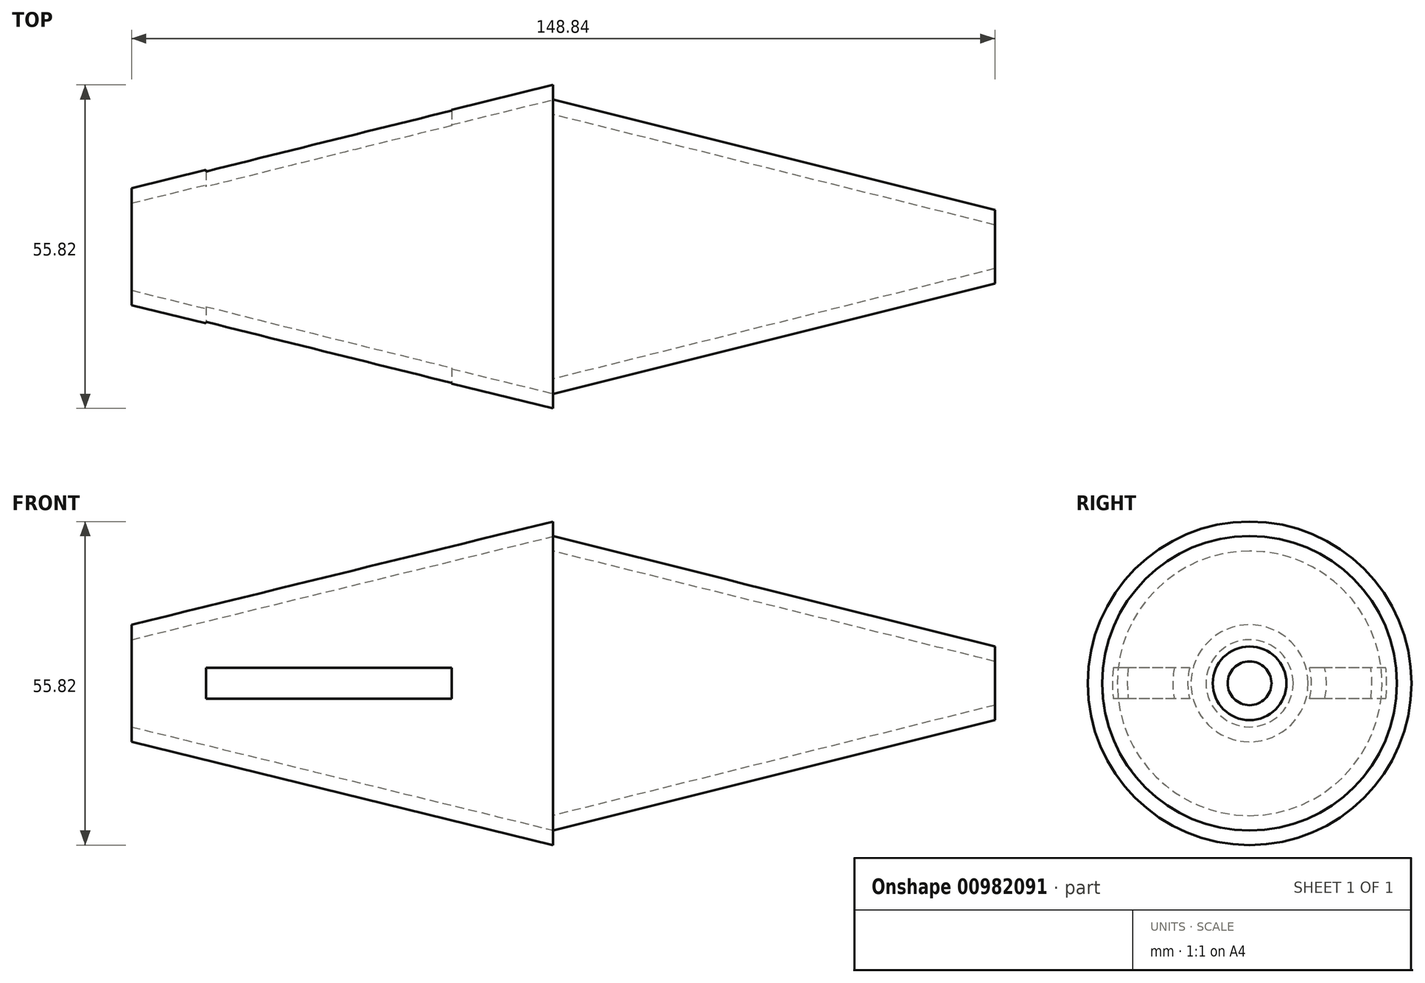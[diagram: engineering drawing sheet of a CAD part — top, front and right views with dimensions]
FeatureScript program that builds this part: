
annotation { "Feature Type Name" : "Feature", "Feature Type Description" : "" }
export const myFeature = defineFeature(function(context is Context, id is Id, definition is map)
    precondition{}
    {
        {
            var Q0;
            Q0=qCreatedBy(makeId("Front.planeOp"),FACE);
            var sketch = newSketch(context, id + "F0", { "sketchPlane" : qUnion([Q0])});
            skLineSegment(sketch, "E0", {"start": v(76.2, 0) * mm, "end": v(76.2, 6.35) * mm});
            skLineSegment(sketch, "E1", {"start": v(76.2, 6.35) * mm, "end": v(0, 25.4) * mm});
            skLineSegment(sketch, "E2", {"start": v(0, 25.4) * mm, "end": v(0, 0) * mm});
            skLineSegment(sketch, "E3", {"start": v(0, 0) * mm, "end": v(76.2, 0) * mm});
            skSolve(sketch);
        }
        {
            var Q0;
            Q0 = qSketchRegion(id + "F0", true);
            var Q1;
            Q1=sQuery(id+"F0.wireOp",EDGE,"E3");
            revolve(context, id + "F1", {"surfaceOperationType" : NewSurfaceOperationType.NEW, "entities" : qUnion([Q0]), "axis" : qUnion([Q1]), "revolveType" : RevolveType.FULL});
        }
        {
            var Q0;
            Q0=makeQuery(id+"F1.opRevolve","SWEPT_FACE",FACE,{"disambiguationData":[OSD([sQuery(id+"F0.wireOp",EDGE,"E2")])]});
            var Q1;
            Q1=makeQuery(id+"F1.opRevolve","SWEPT_FACE",FACE,{"disambiguationData":[OSD([sQuery(id+"F0.wireOp",EDGE,"E0")])]});
            shell(context, id + "F2", {"entities" : qUnion([Q0, Q1]), "thickness" : 2.5 * mm});
        }
        {
            var Q0;
            Q0=qCreatedBy(makeId("Front.planeOp"),FACE);
            var sketch = newSketch(context, id + "F3", { "sketchPlane" : qUnion([Q0])});
            skLineSegment(sketch, "E4", {"start": v(0, 27.91) * mm, "end": v(0, 0) * mm});
            skLineSegment(sketch, "E5", {"start": v(0, 27.91) * mm, "end": v(-72.64, 10.1) * mm});
            skLineSegment(sketch, "E6", {"start": v(-72.64, 10.1) * mm, "end": v(-72.64, 0) * mm});
            skLineSegment(sketch, "E7", {"start": v(-72.64, 0) * mm, "end": v(0, 0) * mm});
            skSolve(sketch);
        }
        {
            var Q0;
            Q0 = qSketchRegion(id + "F3", true);
            var Q1;
            Q1=sQuery(id+"F3.wireOp",EDGE,"E7");
            revolve(context, id + "F4", {"surfaceOperationType" : NewSurfaceOperationType.NEW, "entities" : qUnion([Q0]), "axis" : qUnion([Q1]), "revolveType" : RevolveType.FULL});
        }
        {
            var Q0;
            Q0=makeQuery(id+"F4.opRevolve","SWEPT_FACE",FACE,{"disambiguationData":[OSD([sQuery(id+"F3.wireOp",EDGE,"E6")])]});
            var Q1;
            Q1=makeQuery(id+"F4.opRevolve","SWEPT_FACE",FACE,{"disambiguationData":[OSD([sQuery(id+"F3.wireOp",EDGE,"E4")])]});
            shell(context, id + "F5", {"entities" : qUnion([Q0, Q1]), "thickness" : 2.5 * mm});
        }
        {
            var Q0;
            Q0=qCreatedBy(makeId("Front.planeOp"),FACE);
            var sketch = newSketch(context, id + "F6", { "sketchPlane" : qUnion([Q0])});
            skLineSegment(sketch, "E8.bottom", {"start": v(-17.42, 2.68) * mm, "end": v(-59.83, 2.68) * mm});
            skLineSegment(sketch, "E8.top", {"start": v(-17.42, -2.68) * mm, "end": v(-59.83, -2.68) * mm});
            skLineSegment(sketch, "E8.left", {"start": v(-17.42, 2.68) * mm, "end": v(-17.42, -2.68) * mm});
            skLineSegment(sketch, "E8.right", {"start": v(-59.83, 2.68) * mm, "end": v(-59.83, -2.68) * mm});
            skPoint(sketch, "E8.middle", {"position": v(-38.62, 0) * mm});
            skSolve(sketch);
        }
        {
            var Q0;
            Q0 = qSketchRegion(id + "F6", true);
            extrude(context, id + "F7", {"entities" : qUnion([Q0]), "operationType" : NewBodyOperationType.REMOVE, "oppositeDirection" : true, "depth" : 25 * mm, "offsetDistance" : 25 * mm, "hasSecondDirection" : true, "secondDirectionOppositeDirection" : false, "secondDirectionDepth" : 25 * mm});
        }
    });
